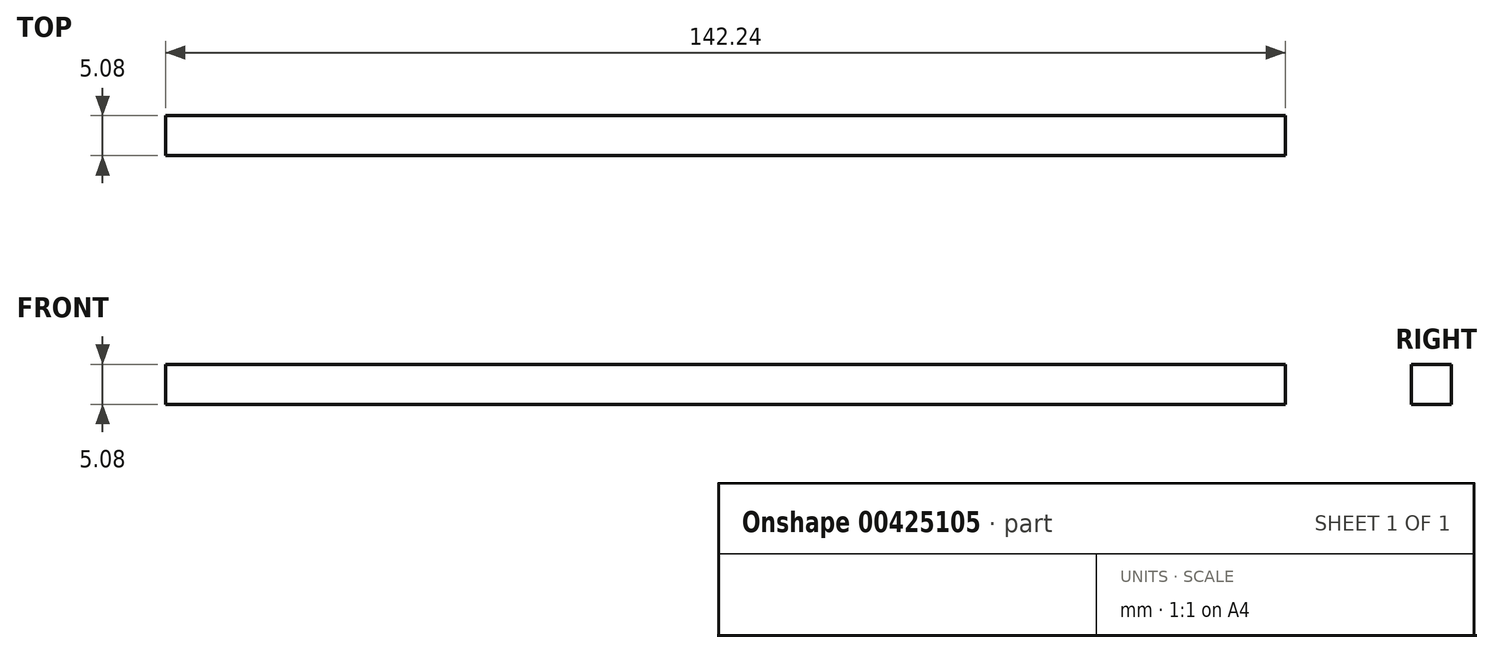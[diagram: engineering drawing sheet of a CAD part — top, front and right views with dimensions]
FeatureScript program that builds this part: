
annotation { "Feature Type Name" : "Feature", "Feature Type Description" : "" }
export const myFeature = defineFeature(function(context is Context, id is Id, definition is map)
    precondition{}
    {
        {
            var Q0;
            Q0=qCreatedBy(makeId("Front.planeOp"),FACE);
            var sketch = newSketch(context, id + "F0", { "sketchPlane" : qUnion([Q0])});
            skLineSegment(sketch, "E0.bottom", {"start": v(-63.6, -25.15) * mm, "end": v(78.65, -25.15) * mm});
            skLineSegment(sketch, "E0.top", {"start": v(-63.6, -30.23) * mm, "end": v(78.65, -30.23) * mm});
            skLineSegment(sketch, "E0.left", {"start": v(-63.6, -25.15) * mm, "end": v(-63.6, -30.23) * mm});
            skLineSegment(sketch, "E0.right", {"start": v(78.65, -25.15) * mm, "end": v(78.65, -30.23) * mm});
            skSolve(sketch);
        }
        {
            var Q0;
            Q0 = qSketchRegion(id + "F0", true);
            extrude(context, id + "F1", {"entities" : qUnion([Q0]), "depth" : 5.08 * mm});
        }
    });
